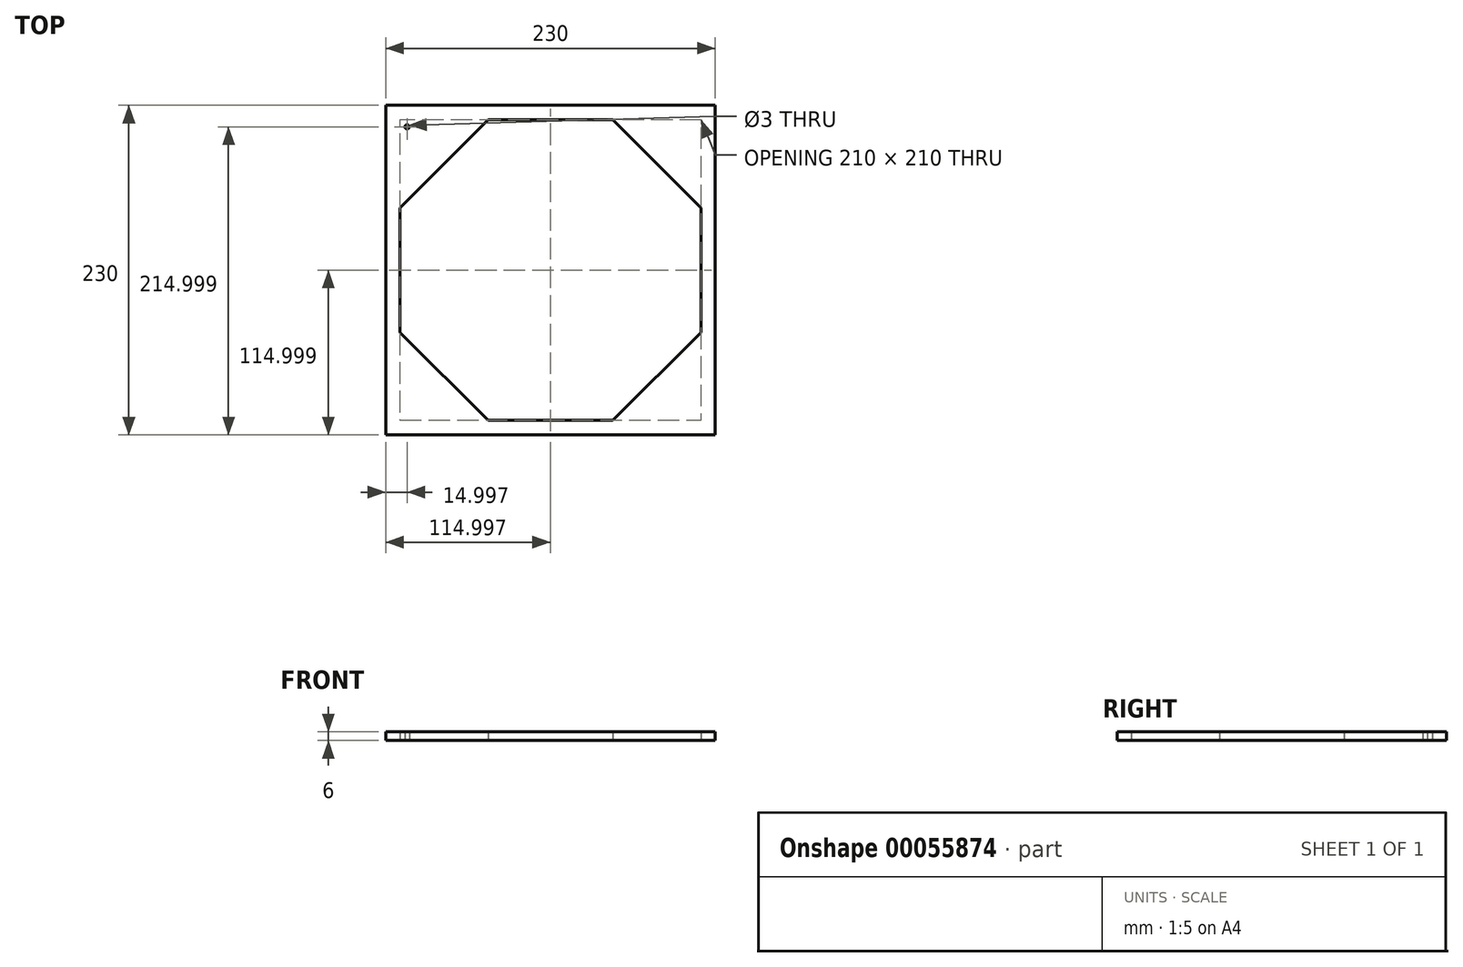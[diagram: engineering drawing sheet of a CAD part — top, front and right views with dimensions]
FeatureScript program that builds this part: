
annotation { "Feature Type Name" : "Feature", "Feature Type Description" : "" }
export const myFeature = defineFeature(function(context is Context, id is Id, definition is map)
    precondition{}
    {
        {
            var Q0;
            Q0=qCreatedBy(makeId("Top.planeOp"),FACE);
            var sketch = newSketch(context, id + "F0", { "sketchPlane" : qUnion([Q0])});
            skCircle(sketch, "E0.cCircle", {"center": v(-297.8, 119.86) * mm, "radius": 100 * mm, "construction": true});
            skLineSegment(sketch, "E0.0", {"start": v(-339.21, 219.86) * mm, "end": v(-256.37, 219.86) * mm});
            skLineSegment(sketch, "E0.1", {"start": v(-256.37, 219.86) * mm, "end": v(-197.8, 161.28) * mm});
            skLineSegment(sketch, "E0.2", {"start": v(-197.8, 161.28) * mm, "end": v(-197.8, 78.44) * mm});
            skLineSegment(sketch, "E0.3", {"start": v(-197.8, 78.44) * mm, "end": v(-256.37, 19.86) * mm});
            skLineSegment(sketch, "E0.4", {"start": v(-256.37, 19.86) * mm, "end": v(-339.21, 19.86) * mm});
            skLineSegment(sketch, "E0.5", {"start": v(-339.21, 19.86) * mm, "end": v(-397.8, 78.44) * mm});
            skLineSegment(sketch, "E0.6", {"start": v(-397.8, 78.44) * mm, "end": v(-397.8, 161.28) * mm});
            skLineSegment(sketch, "E0.7", {"start": v(-397.8, 161.28) * mm, "end": v(-339.21, 219.86) * mm});
            skPoint(sketch, "E0.0.midPoint", {"position": v(-297.8, 219.86) * mm});
            skCircle(sketch, "E1", {"center": v(-329.58, 151.65) * mm, "radius": 1.3 * mm, "construction": true});
            skCircle(sketch, "E2", {"center": v(-266, 151.65) * mm, "radius": 1.3 * mm, "construction": true});
            skCircle(sketch, "E3", {"center": v(-329.58, 88.07) * mm, "radius": 1.3 * mm, "construction": true});
            skCircle(sketch, "E4", {"center": v(-266, 88.07) * mm, "radius": 1.3 * mm, "construction": true});
            skLineSegment(sketch, "E5", {"start": v(-297.8, 119.86) * mm, "end": v(-284.2, 119.86) * mm, "construction": true});
            skPoint(sketch, "E6", {"position": v(-297.8, 77) * mm});
            skLineSegment(sketch, "E7", {"start": v(-297.8, 77) * mm, "end": v(-231.12, 77) * mm, "construction": true});
            skLineSegment(sketch, "E8", {"start": v(-297.8, 77) * mm, "end": v(-364.47, 77) * mm, "construction": true});
            skCircle(sketch, "E9", {"center": v(-364.47, 77) * mm, "radius": 3.81 * mm});
            skCircle(sketch, "E10", {"center": v(-231.12, 77) * mm, "radius": 3.81 * mm});
            skLineSegment(sketch, "E11", {"start": v(-297.8, 119.86) * mm, "end": v(-297.8, 77) * mm, "construction": true});
            skLineSegment(sketch, "E12.0", {"start": v(-341.29, 224.86) * mm, "end": v(-254.3, 224.86) * mm});
            skLineSegment(sketch, "E12.1", {"start": v(-402.8, 163.35) * mm, "end": v(-341.29, 224.86) * mm});
            skLineSegment(sketch, "E12.2", {"start": v(-254.3, 224.86) * mm, "end": v(-192.8, 163.35) * mm});
            skLineSegment(sketch, "E12.3", {"start": v(-402.8, 76.37) * mm, "end": v(-402.8, 163.35) * mm});
            skLineSegment(sketch, "E12.5", {"start": v(-192.8, 76.37) * mm, "end": v(-254.3, 14.86) * mm});
            skLineSegment(sketch, "E12.6", {"start": v(-254.3, 14.86) * mm, "end": v(-341.29, 14.86) * mm});
            skLineSegment(sketch, "E12.7", {"start": v(-341.29, 14.86) * mm, "end": v(-402.8, 76.37) * mm});
            skLineSegment(sketch, "E13.1.0.8", {"start": v(-197.8, 78.44) * mm, "end": v(-197.8, 161.28) * mm, "construction": true});
            skLineSegment(sketch, "E14", {"start": v(-192.8, 163.35) * mm, "end": v(-192.8, 76.37) * mm});
            skLineSegment(sketch, "E15.bottom", {"start": v(-182.8, 234.86) * mm, "end": v(-412.8, 234.86) * mm});
            skLineSegment(sketch, "E15.top", {"start": v(-182.8, 4.86) * mm, "end": v(-412.8, 4.86) * mm});
            skLineSegment(sketch, "E15.left", {"start": v(-182.8, 234.86) * mm, "end": v(-182.8, 4.86) * mm});
            skLineSegment(sketch, "E15.right", {"start": v(-412.8, 234.86) * mm, "end": v(-412.8, 4.86) * mm});
            skLineSegment(sketch, "E16", {"start": v(-397.8, 161.28) * mm, "end": v(-397.8, 234.86) * mm, "construction": true});
            skLineSegment(sketch, "E17", {"start": v(-339.21, 219.86) * mm, "end": v(-412.8, 219.86) * mm, "construction": true});
            skCircle(sketch, "E18", {"center": v(-397.8, 219.86) * mm, "radius": 1.5 * mm});
            skSolve(sketch);
        }
        {
            var Q0;
            Q0 = qSketchRegion(id + "F0", true);
            extrude(context, id + "F1", {"entities" : qUnion([Q0]), "depth" : 6 * mm});
        }
    });
